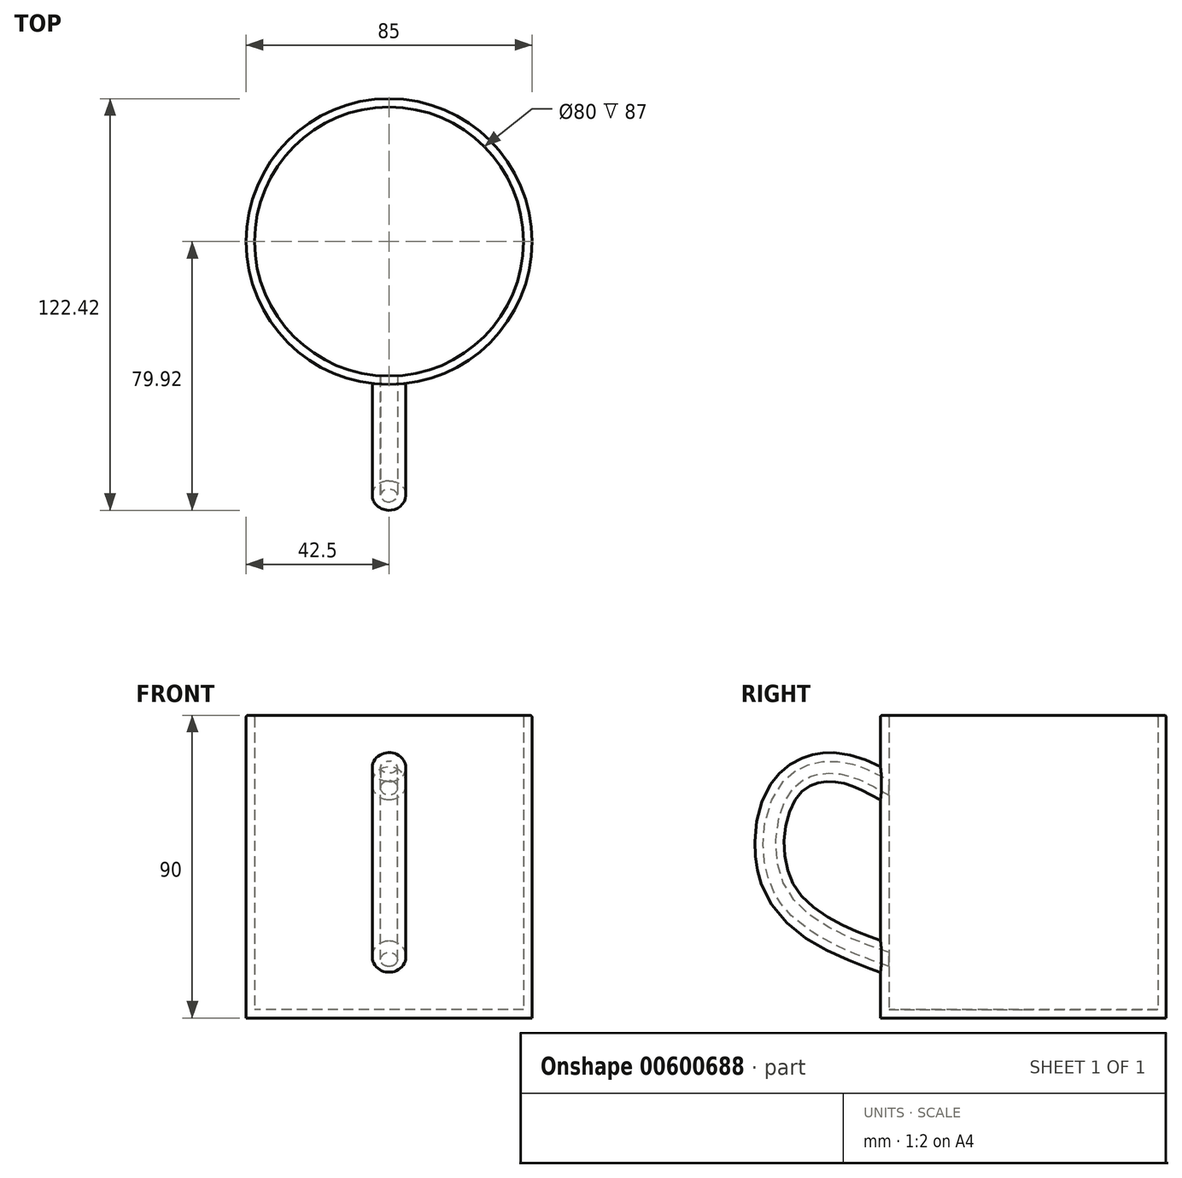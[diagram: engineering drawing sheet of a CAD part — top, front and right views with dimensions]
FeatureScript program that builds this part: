
annotation { "Feature Type Name" : "Feature", "Feature Type Description" : "" }
export const myFeature = defineFeature(function(context is Context, id is Id, definition is map)
    precondition{}
    {
        {
            var Q0;
            Q0=qCreatedBy(makeId("Top.planeOp"),FACE);
            var sketch = newSketch(context, id + "F0", { "sketchPlane" : qUnion([Q0])});
            skCircle(sketch, "E0", {"center": v(0, 0) * mm, "radius": 42.5 * mm});
            skSolve(sketch);
        }
        {
            var Q0;
            Q0 = qSketchRegion(id + "F0", true);
            extrude(context, id + "F1", {"entities" : qUnion([Q0]), "endBound" : BoundingType.SYMMETRIC, "depth" : 90 * mm, "offsetDistance" : 25 * mm});
        }
        {
            var Q0;
            Q0=qCreatedBy(makeId("Front.planeOp"),FACE);
            cPlane(context, id + "F2", {"entities" : qUnion([Q0]), "cplaneType" : CPlaneType.OFFSET, "offset" : 42 * mm, "width" : 150 * mm, "height" : 150 * mm});
        }
        {
            var Q0;
            Q0=qCreatedBy(makeId("Right.planeOp"),FACE);
            var sketch = newSketch(context, id + "F3", { "sketchPlane" : qUnion([Q0])});
            skFitSpline(sketch, "E1", {"points": [v(-38.81, 23.96) * mm, v(-55.35, 30.35) * mm, v(-71.89, 23.21) * mm, v(-71.33, -10.43) * mm, v(-41.63, -28.1) * mm, v(-37.68, -29.79) * mm], "startDerivative": vector(-84.28, 46.2) * mm, "endDerivative": vector(28.9, -14.42) * mm});
            skSolve(sketch);
        }
        {
            var Q0;
            Q0=qCreatedBy(id+"F2.planeOp",FACE);
            var sketch = newSketch(context, id + "F4", { "sketchPlane" : qUnion([Q0])});
            skCircle(sketch, "E2", {"center": v(0, 24.55) * mm, "radius": 5 * mm});
            skSolve(sketch);
        }
        {
            var Q0;
            Q0 = qSketchRegion(id + "F4", true);
            var Q1;
            Q1 = qConstructionFilter(qBodyType(qCreatedBy(id + "F3" ,EDGE), BodyType.WIRE), ConstructionObject.NO);
            sweep(context, id + "F5", {"operationType" : NewBodyOperationType.ADD, "profiles" : qUnion([Q0]), "path" : qUnion([Q1])});
        }
        {
            var Q0;
            Q0=makeQuery(id+"F1.opExtrude","CAP_FACE",FACE,{"disambiguationData":[OSD([sQuery(id+"F0.wireOp",EDGE,"E0")])],"isStart":false});
            shell(context, id + "F6", {"entities" : qUnion([Q0]), "thickness" : 2.5 * mm});
        }
        {
            var Q0;
            {var subQ0=sQuery(id+"F0.wireOp",EDGE,"E0");Q0=makeQuery(id+"F6.opShell","OFFSET_EDGE",EDGE,{"disambiguationData":[OSD([subQ0]),TDD([makeQuery(id+"F1.opExtrude","CAP_EDGE",EDGE,{"disambiguationData":[OSD([subQ0])],"isStart":false})])]});}
            var Q1;
            Q1=makeQuery(id+"F1.opExtrude","CAP_EDGE",EDGE,{"disambiguationData":[OSD([sQuery(id+"F0.wireOp",EDGE,"E0")])],"isStart":false});
            fillet(context, id + "F7", {"entities" : qUnion([Q0, Q1]), "radius" : 0.5 * mm, "tangentPropagation" : true, "allowEdgeOverflow" : false});
        }
    });
